# Revit family: Gaius Basin Right Handed_
name_source: partatom
category: Plumbing Fixtures
revit_build: Autodesk Revit Architecture 2012 (Build: 20110916_2132(x64)
units: mm (PartAtom-declared; Revit-internal decimal feet)

## types (24) — shared parameters
Drain Pipe = Yes
Drain Pipe Material = Chrome - Polished
Manufacturer = Korpinen Oy
Toilet Paper Holder = No
URL = www.korpinen.com
Vent Connection = No
Water Tap = Yes

## per-type parameters (varying)
| type | Basin Type | CW Connection | HW Connection | Model | Waste Connection |
| Original 6202 | Gaius Basin : 6202 - Gaius Original | Yes | Yes | 6202Gaius Original | Yes |
| Original 6202H | Gaius Basin : 6202 H - Gaius Original | Yes | Yes | 6202 H Gaius Original | Yes |
| Original 6202K | Gaius Basin : 6202 K - Gaius Original | Yes | Yes | 6202 K Gaius Original | Yes |
| Original 6202P | Gaius Basin : 6202 P - Gaius Original | Yes | Yes | 6202 P Gaius Original | Yes |
| Plus 62001 | Gaius Basin : 62001 - Gaius Plus | Yes | Yes | 62001 Gaius Plus | Yes |
| Plus 620011H | Gaius Basin : 62001 H - Gaius Plus | Yes | Yes | 62001 H Gaius Plus | Yes |
| Plus 62001K | Gaius Basin : 62001 K - Gaius Plus | Yes | Yes | 62001 K Gaius Plus | Yes |
| Plus 62001P | Gaius Basin : 62001 P - Gaius Plus | Yes | Yes | 62001 P Gaius Plus | Yes |
| Public 62012 | Gaius Basin : 62012 - Gaius Public | Yes | Yes | 62012 Gaius Public | Yes |
| Public 62014 | Gaius Basin : 62014 - Gaius Public | Yes | Yes | 62014 Gaius Public | Yes |
| Original 6202 + 6230 | Gaius Basin : 6202 + 6230 - Gaius Original | Yes | Yes | 6202 + 6230 Gaius Original | Yes |
| Original 6202H + 6230 | Gaius Basin : 6202 H + 6230 - Gaius Original | No | No | 6202 H + 6230 Gaius Original | No |
| Original 6202K + 6230 | Gaius Basin : 6202 K + 6230 - Gaius Original | No | No | 6202 K + 6230 Gaius Original | No |
| Original 6202P + 6230 | Gaius Basin : 6202 P + 6230 - Gaius Original | No | No | 6202 P + 6230 Gaius Original | No |
| Plus 62001 + 6231 | Gaius Basin : 62001 + 6231 - Gaius Plus | Yes | Yes | 62001 + 6231 Gaius Plus | Yes |
| Plus 62001H + 6231 | Gaius Basin : 62001 H + 6231 - Gaius Plus | Yes | Yes | 62001 H + 6231 Gaius Plus | Yes |
| Plus 62001K + 6231 | Gaius Basin : 62001 K + 6231 - Gaius Plus | Yes | Yes | 62001 K + 6231 Gaius Plus | Yes |
| Plus 62001P + 6231 | Gaius Basin : 62001 P + 6231 - Gaius Plus | Yes | Yes | 62001 P + 6231 Gaius Plus | Yes |
| Original 6202 + 6236 | Gaius Basin : 6202 + 6236 - Gaius Original | Yes | Yes | 6202 + 6236 Gaius Original | Yes |
| Original 6202H + 6236 | Gaius Basin : 6202 H + 6236 - Gaius Original | Yes | Yes | 6202 H + 6236 Gaius Original | Yes |
| Original 6202K + 6236 | Gaius Basin : 6202 K + 6236 - Gaius Original | Yes | Yes | 6202 K + 6236 Gaius Original | Yes |
| Original 6202P+ 6236 | Gaius Basin : 6202 P + 6236 - Gaius Original | No | No | 6202 P + 6236 Gaius Original | No |
| Mini 6302 | Gaius Mini : 6302 - Gaius Mini | Yes | Yes | 6302 Gaius Mini | Yes |
| Mini 6302 + 6230 | Gaius Mini : 6302 + 6230 - Gaius Mini | Yes | Yes | 6302 + 6230 Gaius Mini | Yes |

## geometry (parser evidence)
native form markers: Sweep x53
no freeform markers — native parametric forms only
